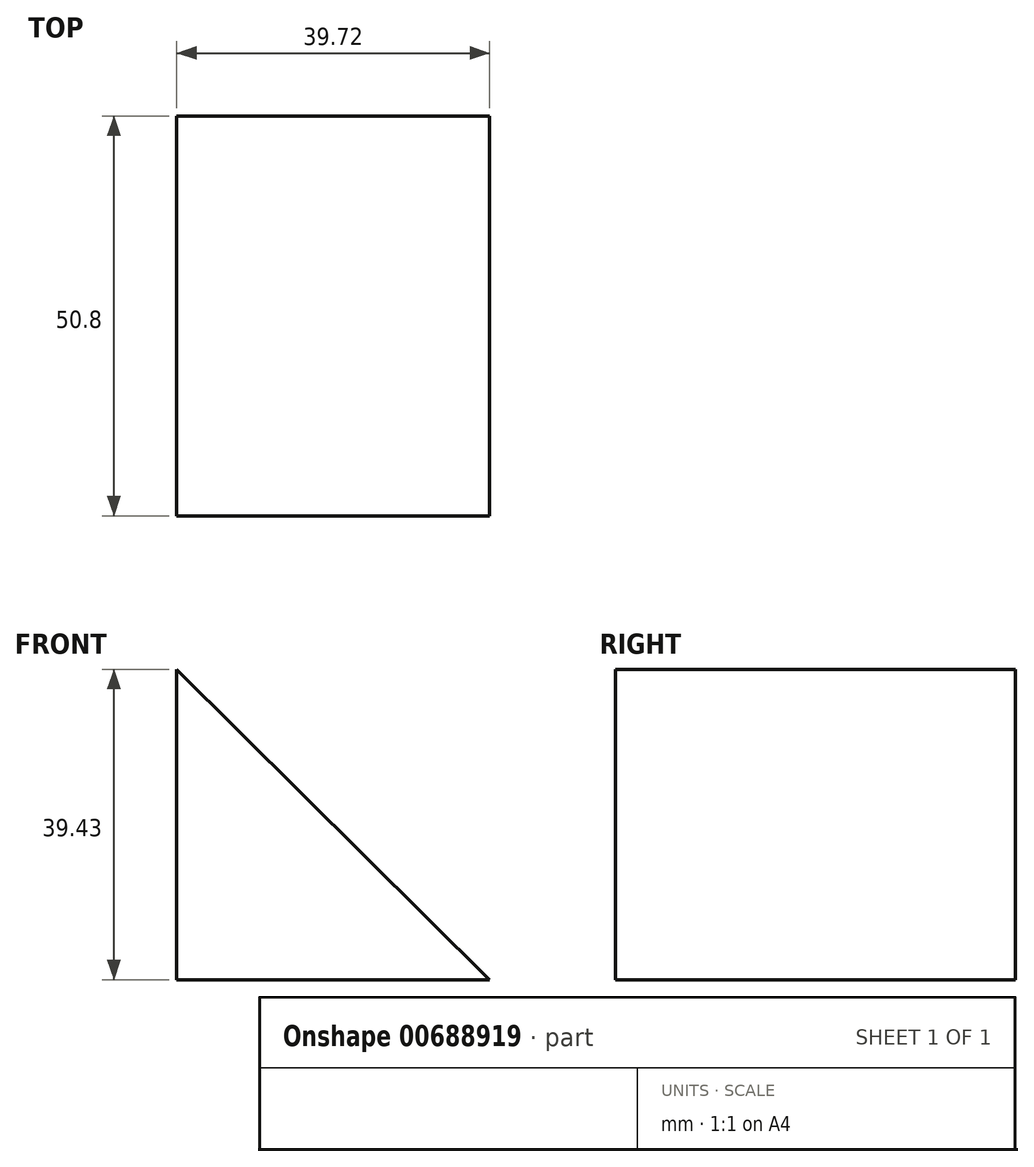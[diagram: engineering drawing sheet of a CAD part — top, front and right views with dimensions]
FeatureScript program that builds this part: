
annotation { "Feature Type Name" : "Feature", "Feature Type Description" : "" }
export const myFeature = defineFeature(function(context is Context, id is Id, definition is map)
    precondition{}
    {
        {
            var Q0;
            Q0=qCreatedBy(makeId("Front.planeOp"),FACE);
            var sketch = newSketch(context, id + "F0", { "sketchPlane" : qUnion([Q0])});
            skLineSegment(sketch, "E0", {"start": v(-28.55, 39.43) * mm, "end": v(-28.55, 0) * mm});
            skLineSegment(sketch, "E1", {"start": v(-28.55, 0) * mm, "end": v(11.17, 0) * mm});
            skLineSegment(sketch, "E2", {"start": v(-28.55, 39.43) * mm, "end": v(11.17, 0) * mm});
            skSolve(sketch);
        }
        {
            var Q0;
            Q0 = qSketchRegion(id + "F0", true);
            extrude(context, id + "F1", {"entities" : qUnion([Q0]), "depth" : 50.8 * mm, "offsetDistance" : 25.4 * mm});
        }
    });
